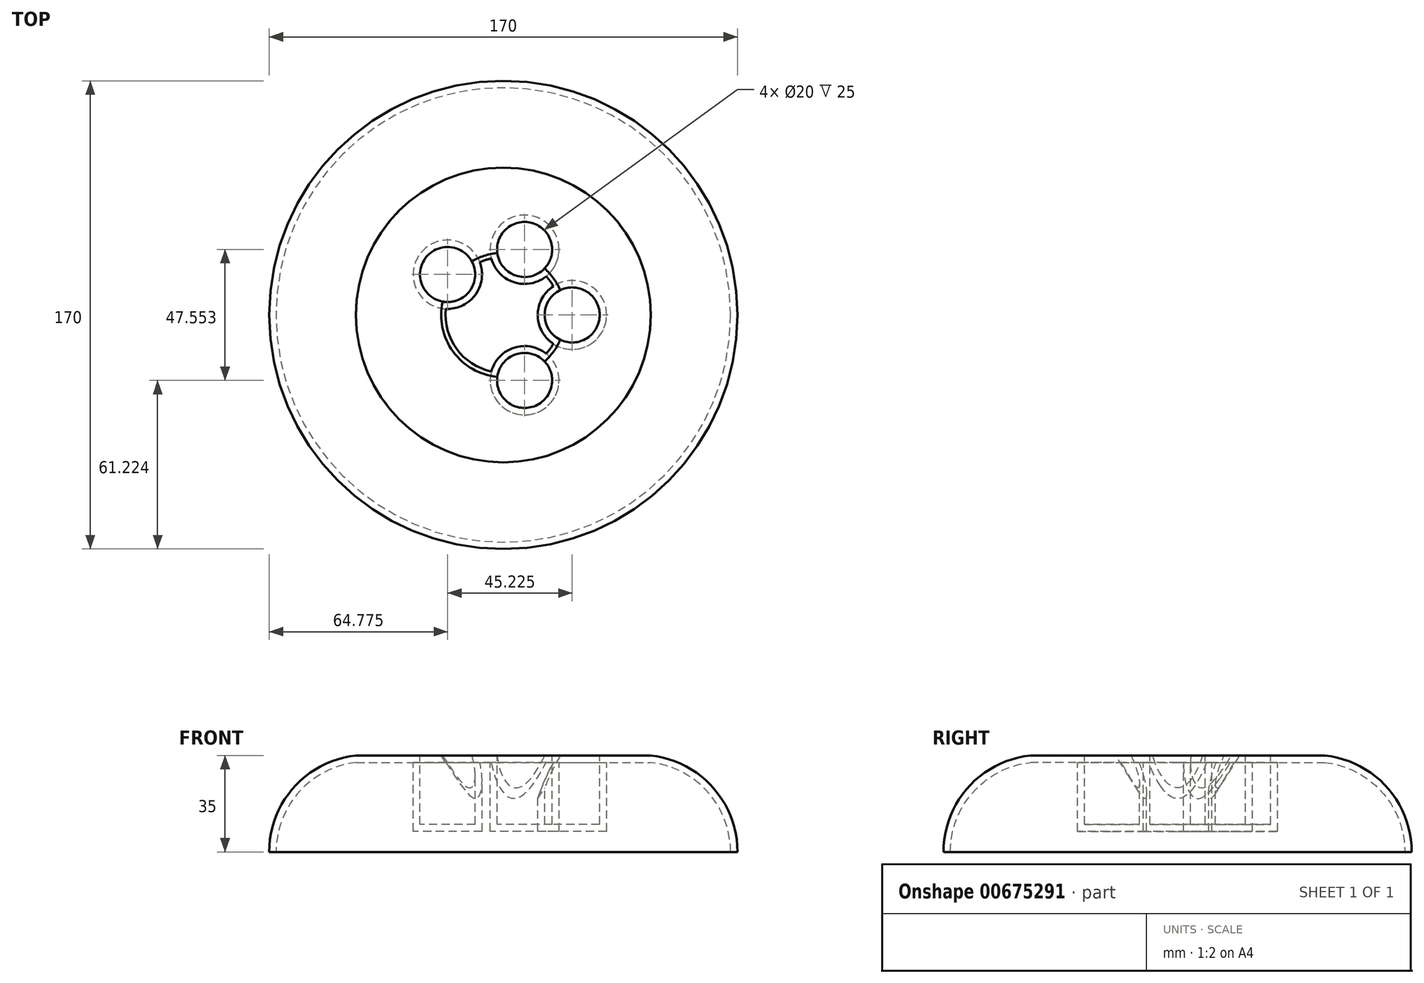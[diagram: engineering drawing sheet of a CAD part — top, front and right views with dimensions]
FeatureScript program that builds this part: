
annotation { "Feature Type Name" : "Feature", "Feature Type Description" : "" }
export const myFeature = defineFeature(function(context is Context, id is Id, definition is map)
    precondition{}
    {
        {
            var Q0;
            Q0=qCreatedBy(makeId("Front.planeOp"),FACE);
            var sketch = newSketch(context, id + "F0", { "sketchPlane" : qUnion([Q0])});
            skLineSegment(sketch, "E0", {"start": v(0, 0) * mm, "end": v(85, 0) * mm});
            skArc(sketch, "E1", {"start": v(85, 0) * mm, "mid": v(75.97, 23.54) * mm, "end": v(53.52, 35) * mm});
            skLineSegment(sketch, "E2", {"start": v(85, 0) * mm, "end": v(85, -45.57) * mm, "construction": true});
            skLineSegment(sketch, "E3", {"start": v(53.52, 35) * mm, "end": v(0, 35) * mm});
            skLineSegment(sketch, "E4", {"start": v(0, 35) * mm, "end": v(0, 0) * mm});
            skSolve(sketch);
        }
        {
            var Q0;
            Q0=makeQuery(id+"F0.imprint","IMPRINT",FACE,{"disambiguationData":[TD([[makeQuery(id+"F0.imprint","IMPRINT",EDGE,{"derivedFrom":sQuery(id+"F0.wireOp",EDGE,"E0")}),1.0]])]});
            var Q1;
            Q1=sQuery(id+"F0.wireOp",EDGE,"E4");
            revolve(context, id + "F1", {"entities" : qUnion([Q0]), "axis" : qUnion([Q1]), "revolveType" : RevolveType.FULL});
        }
        {
            var Q0;
            Q0=makeQuery(id+"F1.opRevolve","SWEPT_FACE",FACE,{"disambiguationData":[OSD([sQuery(id+"F0.wireOp",EDGE,"E3")])]});
            var sketch = newSketch(context, id + "F2", { "sketchPlane" : qUnion([Q0])});
            skCircle(sketch, "E5", {"center": v(25, 0) * mm, "radius": 10 * mm});
            skCircle(sketch, "E6.1.0", {"center": v(7.73, 23.78) * mm, "radius": 10 * mm});
            skCircle(sketch, "E6.2.0", {"center": v(-20.23, 14.7) * mm, "radius": 10 * mm});
            skCircle(sketch, "E6.3.0", {"center": v(-20.23, -14.7) * mm, "radius": 10 * mm});
            skCircle(sketch, "E6.4.0", {"center": v(7.73, -23.78) * mm, "radius": 10 * mm});
            skPoint(sketch, "E6.center", {"position": v(0, 0) * mm});
            skSolve(sketch);
        }
        {
            var Q0;
            Q0=makeQuery(id+"F2.imprint","IMPRINT",FACE,{"disambiguationData":[TD([[makeQuery(id+"F2.imprint","IMPRINT",EDGE,{"derivedFrom":sQuery(id+"F2.wireOp",EDGE,"E6.1.0")}),1.0]])]});
            var Q1;
            Q1=makeQuery(id+"F2.imprint","IMPRINT",FACE,{"disambiguationData":[TD([[makeQuery(id+"F2.imprint","IMPRINT",EDGE,{"derivedFrom":sQuery(id+"F2.wireOp",EDGE,"E5")}),1.0]])]});
            var Q2;
            Q2=makeQuery(id+"F2.imprint","IMPRINT",FACE,{"disambiguationData":[TD([[makeQuery(id+"F2.imprint","IMPRINT",EDGE,{"derivedFrom":sQuery(id+"F2.wireOp",EDGE,"E6.4.0")}),1.0]])]});
            var Q3;
            Q3=makeQuery(id+"F2.imprint","IMPRINT",FACE,{"disambiguationData":[TD([[makeQuery(id+"F2.imprint","IMPRINT",EDGE,{"derivedFrom":sQuery(id+"F2.wireOp",EDGE,"E6.2.0")}),1.0]])]});
            extrude(context, id + "F3", {"entities" : qUnion([Q0, Q1, Q2, Q3]), "operationType" : NewBodyOperationType.REMOVE, "oppositeDirection" : true, "depth" : 25 * mm, "offsetDistance" : 25 * mm});
        }
        {
            var Q0;
            Q0=makeQuery(id+"F1.opRevolve","SWEPT_FACE",FACE,{"disambiguationData":[OSD([sQuery(id+"F0.wireOp",EDGE,"E0")])]});
            shell(context, id + "F4", {"entities" : qUnion([Q0]), "thickness" : 2.5 * mm});
        }
        {
            var Q0;
            Q0=qCreatedBy(makeId("Right.planeOp"),FACE);
            var sketch = newSketch(context, id + "F5", { "sketchPlane" : qUnion([Q0])});
            skLineSegment(sketch, "E7", {"start": v(0, 62.83) * mm, "end": v(40.54, 62.83) * mm});
            skLineSegment(sketch, "E8", {"start": v(40.54, 62.83) * mm, "end": v(0, 0) * mm});
            skLineSegment(sketch, "E9", {"start": v(0, 0) * mm, "end": v(0, 62.83) * mm});
            skSolve(sketch);
        }
        {
            var Q0;
            Q0 = qSketchRegion(id + "F5", true);
            var Q1;
            Q1=sQuery(id+"F5.wireOp",EDGE,"E9");
            revolve(context, id + "F6", {"operationType" : NewBodyOperationType.REMOVE, "entities" : qUnion([Q0]), "axis" : qUnion([Q1]), "revolveType" : RevolveType.FULL, "oppositeDirection" : true});
        }
    });
